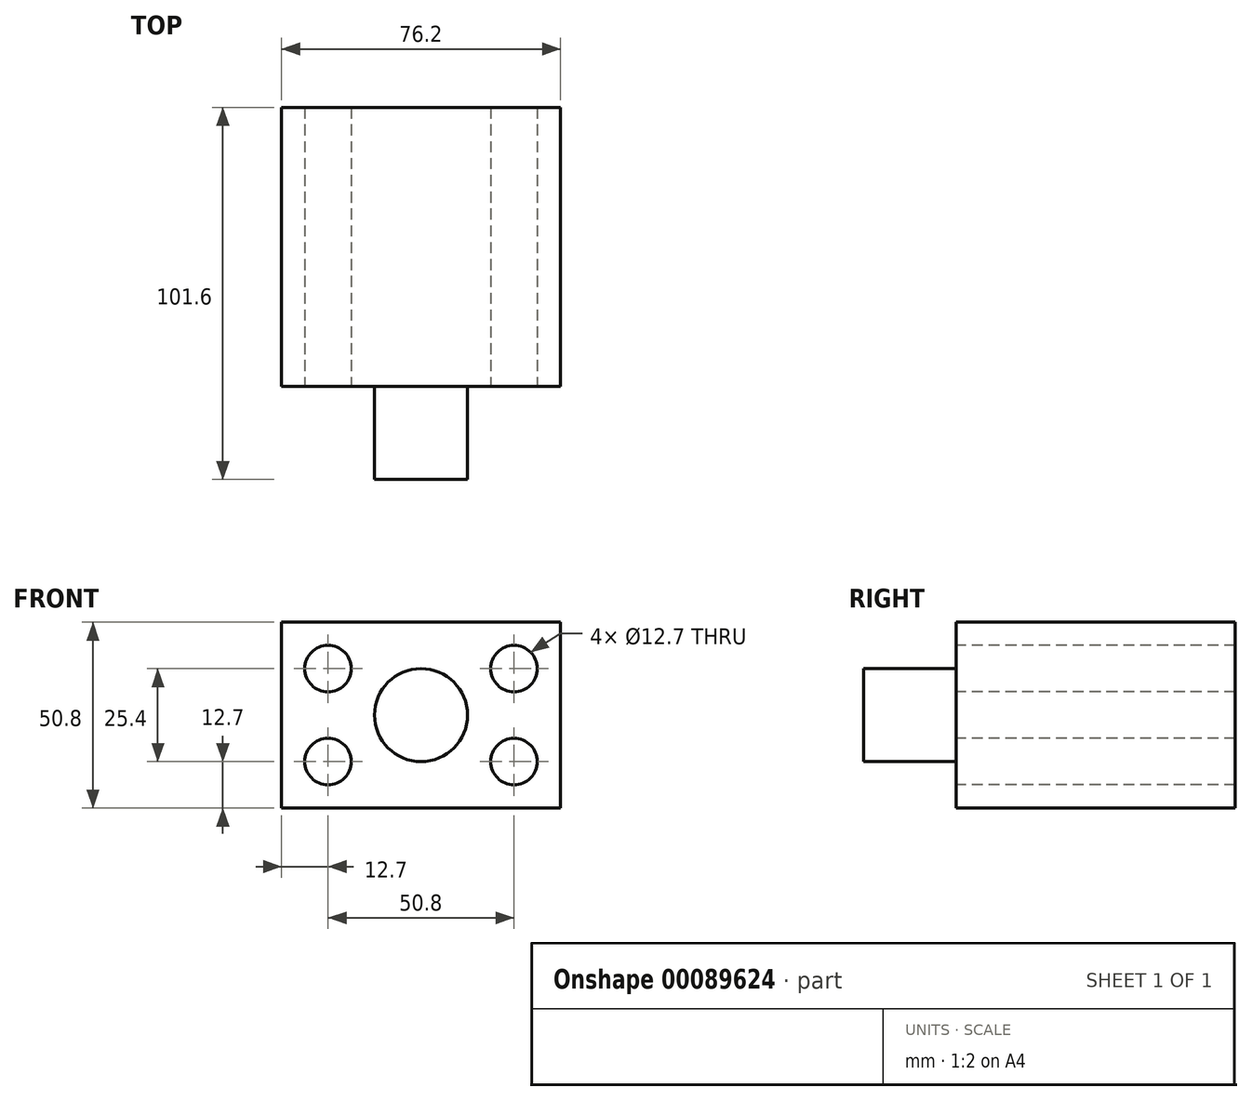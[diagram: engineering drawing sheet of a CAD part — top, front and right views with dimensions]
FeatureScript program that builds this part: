
annotation { "Feature Type Name" : "Feature", "Feature Type Description" : "" }
export const myFeature = defineFeature(function(context is Context, id is Id, definition is map)
    precondition{}
    {
        {
            var Q0;
            Q0=qCreatedBy(makeId("Front.planeOp"),FACE);
            var sketch = newSketch(context, id + "F0", { "sketchPlane" : qUnion([Q0])});
            skLineSegment(sketch, "E0.bottom", {"start": v(-38.1, 25.4) * mm, "end": v(38.1, 25.4) * mm});
            skLineSegment(sketch, "E0.top", {"start": v(-38.1, -25.4) * mm, "end": v(38.1, -25.4) * mm});
            skLineSegment(sketch, "E0.left", {"start": v(-38.1, 25.4) * mm, "end": v(-38.1, -25.4) * mm});
            skLineSegment(sketch, "E0.right", {"start": v(38.1, 25.4) * mm, "end": v(38.1, -25.4) * mm});
            skSolve(sketch);
        }
        {
            var Q0;
            Q0 = qSketchRegion(id + "F0", true);
            extrude(context, id + "F1", {"entities" : qUnion([Q0]), "depth" : 76.2 * mm});
        }
        {
            var Q0;
            Q0=makeQuery(id+"F1.opExtrude","CAP_FACE",FACE,{"disambiguationData":[OSD([sQuery(id+"F0.wireOp",EDGE,"E0.bottom"),sQuery(id+"F0.wireOp",EDGE,"E0.top"),sQuery(id+"F0.wireOp",EDGE,"E0.left"),sQuery(id+"F0.wireOp",EDGE,"E0.right")])],"isStart":false});
            var sketch = newSketch(context, id + "F2", { "sketchPlane" : qUnion([Q0])});
            skCircle(sketch, "E1", {"center": v(-25.4, 12.7) * mm, "radius": 6.35 * mm});
            skCircle(sketch, "E2", {"center": v(-25.4, -12.7) * mm, "radius": 6.35 * mm});
            skCircle(sketch, "E3", {"center": v(25.4, 12.7) * mm, "radius": 6.35 * mm});
            skCircle(sketch, "E4", {"center": v(25.4, -12.7) * mm, "radius": 6.35 * mm});
            skSolve(sketch);
        }
        {
            var Q0;
            Q0 = qSketchRegion(id + "F2", true);
            extrude(context, id + "F3", {"entities" : qUnion([Q0]), "operationType" : NewBodyOperationType.REMOVE, "endBound" : BoundingType.THROUGH_ALL, "oppositeDirection" : true, "depth" : 25.4 * mm});
        }
        {
            var Q0;
            Q0=qCreatedBy(makeId("Top.planeOp"),FACE);
            var sketch = newSketch(context, id + "F4", { "sketchPlane" : qUnion([Q0])});
            skLineSegment(sketch, "E5.bottom", {"start": v(0, -76.2) * mm, "end": v(-12.7, -76.2) * mm});
            skLineSegment(sketch, "E5.top", {"start": v(0, -101.6) * mm, "end": v(-12.7, -101.6) * mm});
            skLineSegment(sketch, "E5.left", {"start": v(0, -76.2) * mm, "end": v(0, -101.6) * mm});
            skLineSegment(sketch, "E5.right", {"start": v(-12.7, -76.2) * mm, "end": v(-12.7, -101.6) * mm});
            skSolve(sketch);
        }
        {
            var Q0;
            Q0 = qSketchRegion(id + "F4", true);
            var Q1;
            Q1=sQuery(id+"F4.wireOp",EDGE,"E5.left");
            revolve(context, id + "F5", {"operationType" : NewBodyOperationType.ADD, "entities" : qUnion([Q0]), "axis" : qUnion([Q1]), "revolveType" : RevolveType.FULL});
        }
        {
            var Q0;
            Q0=qCreatedBy(makeId("Top.planeOp"),FACE);
            var sketch = newSketch(context, id + "F6", { "sketchPlane" : qUnion([Q0])});
            skLineSegment(sketch, "E6", {"start": v(12.7, -76.2) * mm, "end": v(12.7, -101.6) * mm});
            skLineSegment(sketch, "E7", {"start": v(-12.7, -101.6) * mm, "end": v(-12.7, -76.2) * mm});
            skLineSegment(sketch, "E8", {"start": v(0, -104.82) * mm, "end": v(0, -74.92) * mm});
            skLineSegment(sketch, "E9", {"start": v(-12.7, -92.04) * mm, "end": v(-7.79, -92.04) * mm});
            skLineSegment(sketch, "E10", {"start": v(-7.79, -92.04) * mm, "end": v(-7.79, -87.02) * mm});
            skLineSegment(sketch, "E11", {"start": v(-7.79, -87.02) * mm, "end": v(-12.7, -87.02) * mm});
            skSolve(sketch);
        }
    });
